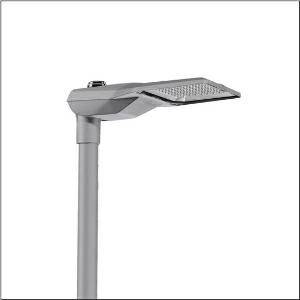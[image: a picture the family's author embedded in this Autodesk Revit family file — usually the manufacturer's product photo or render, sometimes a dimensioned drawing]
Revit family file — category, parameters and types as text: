
# Revit family: streetlight_sl_21_midi___st0_8a_5xe7c47n08lb_a78e
name_source: partatom
category: Lighting Fixtures
units: mm (PartAtom-declared; Revit-internal decimal feet)

## family parameters
Cut with Voids When Loaded = No
Host = Face
Light Source = No
Part Type = Normal
Room Calculation Point = No
Round Connector Dimension = Use Diameter
Shared = No

## types (1)
- --- (1 x LED, 14950 lm, 98.3 W, 4000K)
    Apparent Load = 98 VA
    CIE Flux Codes = 38 75 97 100 100
    Color Rendering = 70
    Color Temperature = 4000K
    Default Elevation = 1800 mm
    Description = Streetlight SL 21 midi, mast luminaire, primary light control with lens, of PMMA, primary optical cover: cover, of toughened safety glass, transparent, light distribution: ST0.8a, light emission: direct distribution, primary light characteristic: asymmetric, installation type: side-entry, LED, 3G 2.5mm², High Power LED, rated luminous flux: 14.950lm, luminous efficacy: 152lm/W, light colour: 740, colour temperature: 4000K, control: overheat protection, presetting dimming linear, constant luminous flux control, time-dependent luminous flux control, flexible luminous flux parameterisation, mains connection: 220..240V, AC, 50/60Hz, connection cable pre-assembled, cable length: 10,5m, wiring characteristics: H05VV-F, start of lifetime: 98W, end of service life: 101W, reduction: 45W, luminaire housing, of diecast aluminium (EN AC-44300), powder-coated, Siteco® metallic grey (DB 702S), corrosivity category C5 mid according to DIN EN ISO 12944, multi-level sealing system, sealing non-destructively replaceable, inclination adjustable: 0°, 5°, 10°, 15°, length: 644mm, width: 335mm, height: 110mm, spigot size: 42mm (side-entry), protection rating (complete): IP66, insulation class (complete): insulation class I (protective earthing), certification: CE, ENEC, ENEC+, VDE, impact resistance: IK09, permissible operating ambient temperature for outdoor applications: -40..+50°C, standard-compliant lighting for roads and squares, packaging unit: 1 piece

Light Distribution: ST0.8a
    Height = 111 mm
    Lamp = 1 x LED
    Lamp Light Flux = 14950 lm
    Lamp Power = 98.3 W
    Lamp count = 1
    Length = 644 mm
    Luminous efficacy = 152 lm/W
    Manufacturer = Siteco
    ModVariant = No
    Model = 5XE7C47N08LB
    Number of Poles = 1
    OnlyDefault = Yes
    Power Factor = 1
    Product Name = Streetlight SL 21 midi | ST0.8a
    Product group = mast luminaire | pylon top
    ProductGroupID = 6100
    Protection Class = Protection class I
    Protection Degree = IP 66
    RLX_Detail_Level = 1
    RLX_Emergency_Light_Flux = 0 lm
    RLX_Emergency_Type = 0
    RLX_Emergency_Type_DB = No
    RlxData = <blob elided: 90569 chars, md5=60f458ac>
    Socket = socket
    Standby Power = 0 W
    System Light Flux = 14950 lm
    System Power = 98 W
    Type Comments = factory setting: luminous flux: 100 % | dim-lin: 254 | 1020 mA
    Type Image = l_1294377.jpg
    URL = http://relux.com
    VarID = @adj_083407
    Voltage = 0 V
    Weight = 0.00 kg
    Width = 336 mm

## geometry (parser evidence)
native form markers: Blend x4, Sweep x10
no freeform markers — native parametric forms only
